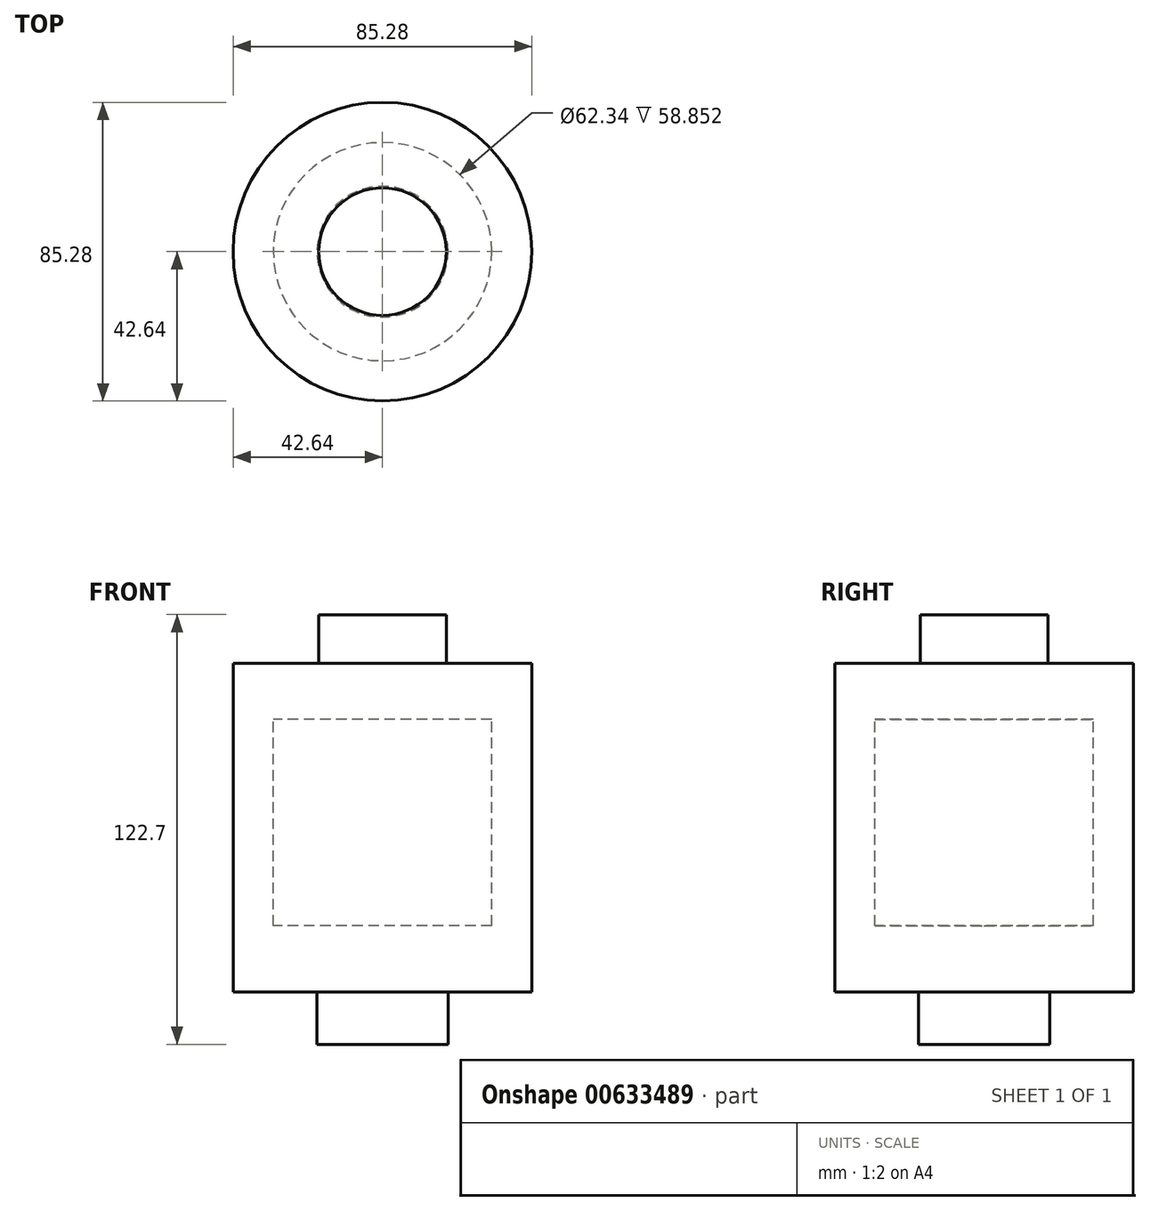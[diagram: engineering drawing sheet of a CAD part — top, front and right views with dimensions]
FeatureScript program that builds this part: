
annotation { "Feature Type Name" : "Feature", "Feature Type Description" : "" }
export const myFeature = defineFeature(function(context is Context, id is Id, definition is map)
    precondition{}
    {
        {
            var Q0;
            Q0=qCreatedBy(makeId("Front.planeOp"),FACE);
            var sketch = newSketch(context, id + "F0", { "sketchPlane" : qUnion([Q0])});
            skLineSegment(sketch, "E0", {"start": v(-18.2, 61.35) * mm, "end": v(-18.2, 47.38) * mm});
            skLineSegment(sketch, "E1", {"start": v(-18.2, 47.38) * mm, "end": v(-42.64, 47.38) * mm});
            skLineSegment(sketch, "E2", {"start": v(-42.64, 47.38) * mm, "end": v(-42.64, 0) * mm});
            skLineSegment(sketch, "E3", {"start": v(-42.64, 0) * mm, "end": v(-42.64, -46.38) * mm});
            skLineSegment(sketch, "E4", {"start": v(-42.64, -46.38) * mm, "end": v(-18.7, -46.38) * mm});
            skLineSegment(sketch, "E5", {"start": v(-18.7, -46.38) * mm, "end": v(-18.7, -61.35) * mm});
            skLineSegment(sketch, "E6", {"start": v(-18.7, -61.35) * mm, "end": v(0, -61.35) * mm});
            skLineSegment(sketch, "E7", {"start": v(-18.2, 61.35) * mm, "end": v(0, 61.35) * mm});
            skLineSegment(sketch, "E8", {"start": v(0, 61.35) * mm, "end": v(0, 31.42) * mm});
            skLineSegment(sketch, "E9", {"start": v(0, 31.42) * mm, "end": v(-31.17, 31.42) * mm});
            skLineSegment(sketch, "E10", {"start": v(-31.17, 31.42) * mm, "end": v(-31.17, -27.43) * mm});
            skLineSegment(sketch, "E11", {"start": v(-31.17, -27.43) * mm, "end": v(0, -27.43) * mm});
            skLineSegment(sketch, "E12", {"start": v(0, -27.43) * mm, "end": v(0, -61.35) * mm});
            skSolve(sketch);
        }
        {
            var Q0;
            Q0=makeQuery(id+"F0.imprint","IMPRINT",FACE,{"disambiguationData":[TD([[makeQuery(id+"F0.imprint","IMPRINT",EDGE,{"derivedFrom":sQuery(id+"F0.wireOp",EDGE,"E0")}),1.0]])]});
            var Q1;
            Q1=sQuery(id+"F0.wireOp",EDGE,"E8");
            revolve(context, id + "F1", {"entities" : qUnion([Q0]), "axis" : qUnion([Q1]), "revolveType" : RevolveType.FULL});
        }
    });
